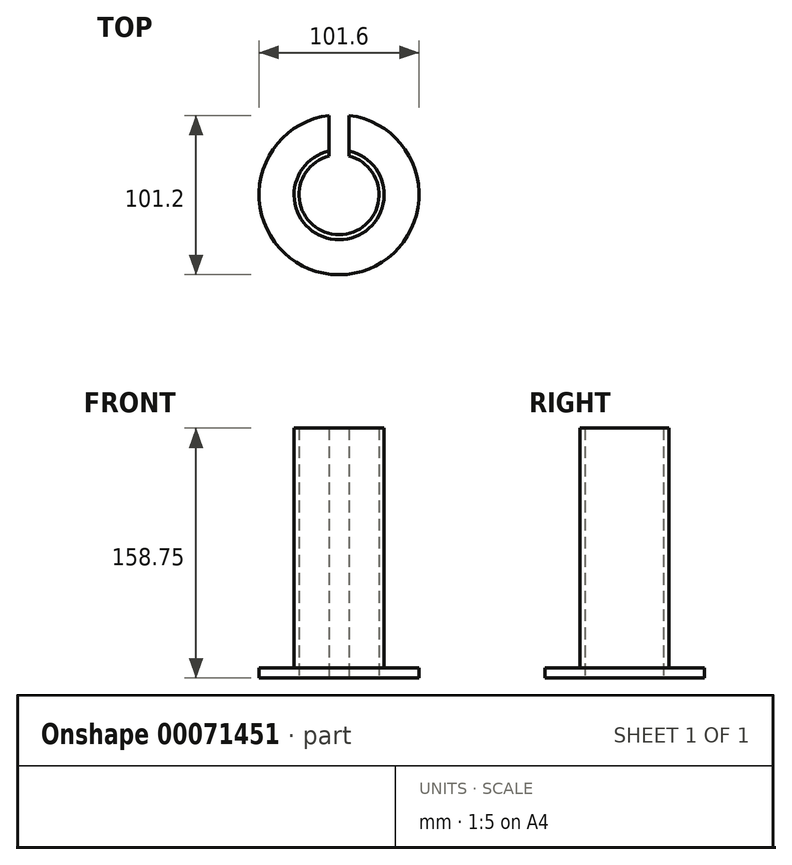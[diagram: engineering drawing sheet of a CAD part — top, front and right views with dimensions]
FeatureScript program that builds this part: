
annotation { "Feature Type Name" : "Feature", "Feature Type Description" : "" }
export const myFeature = defineFeature(function(context is Context, id is Id, definition is map)
    precondition{}
    {
        {
            var Q0;
            Q0=qCreatedBy(makeId("Top.planeOp"),FACE);
            var sketch = newSketch(context, id + "F0", { "sketchPlane" : qUnion([Q0])});
            skCircle(sketch, "E0", {"center": v(0, 0) * mm, "radius": 50.8 * mm});
            skCircle(sketch, "E1", {"center": v(0, 0) * mm, "radius": 25.4 * mm});
            skSolve(sketch);
        }
        {
            var Q0;
            Q0 = qSketchRegion(id + "F0", true);
            extrude(context, id + "F1", {"entities" : qUnion([Q0]), "depth" : 6.35 * mm});
        }
        {
            var Q0;
            Q0=makeQuery(id+"F1.opExtrude","CAP_FACE",FACE,{"disambiguationData":[OSD([sQuery(id+"F0.wireOp",EDGE,"E0"),sQuery(id+"F0.wireOp",EDGE,"E1")])],"isStart":false});
            var sketch = newSketch(context, id + "F2", { "sketchPlane" : qUnion([Q0])});
            skCircle(sketch, "E2", {"center": v(0, 0) * mm, "radius": 25.4 * mm});
            skCircle(sketch, "E3", {"center": v(0, 0) * mm, "radius": 28.58 * mm});
            skSolve(sketch);
        }
        {
            var Q0;
            Q0=makeQuery(id+"F2.imprint","IMPRINT",FACE,{"disambiguationData":[TD([[makeQuery(id+"F2.imprint","IMPRINT",EDGE,{"derivedFrom":sQuery(id+"F2.wireOp",EDGE,"E2")}),-1.0]])]});
            extrude(context, id + "F3", {"entities" : qUnion([Q0]), "operationType" : NewBodyOperationType.ADD, "depth" : 152.4 * mm});
        }
        {
            var Q0;
            Q0=makeQuery(id+"F1.opExtrude","CAP_FACE",FACE,{"disambiguationData":[OSD([sQuery(id+"F0.wireOp",EDGE,"E0"),sQuery(id+"F0.wireOp",EDGE,"E1")])],"isStart":true});
            var sketch = newSketch(context, id + "F4", { "sketchPlane" : qUnion([Q0])});
            skLineSegment(sketch, "E4", {"start": v(0, 50.8) * mm, "end": v(0, -50.8) * mm, "construction": true});
            skLineSegment(sketch, "E5.bottom", {"start": v(-6.35, -13.43) * mm, "end": v(6.35, -13.43) * mm});
            skLineSegment(sketch, "E5.top", {"start": v(-6.35, -64.86) * mm, "end": v(6.35, -64.86) * mm});
            skLineSegment(sketch, "E5.left", {"start": v(-6.35, -13.43) * mm, "end": v(-6.35, -64.86) * mm});
            skLineSegment(sketch, "E5.right", {"start": v(6.35, -13.43) * mm, "end": v(6.35, -64.86) * mm});
            skSolve(sketch);
        }
        {
            var Q0;
            Q0 = qSketchRegion(id + "F4", true);
            extrude(context, id + "F5", {"entities" : qUnion([Q0]), "operationType" : NewBodyOperationType.REMOVE, "endBound" : BoundingType.THROUGH_ALL, "oppositeDirection" : true, "depth" : 25.4 * mm});
        }
    });
